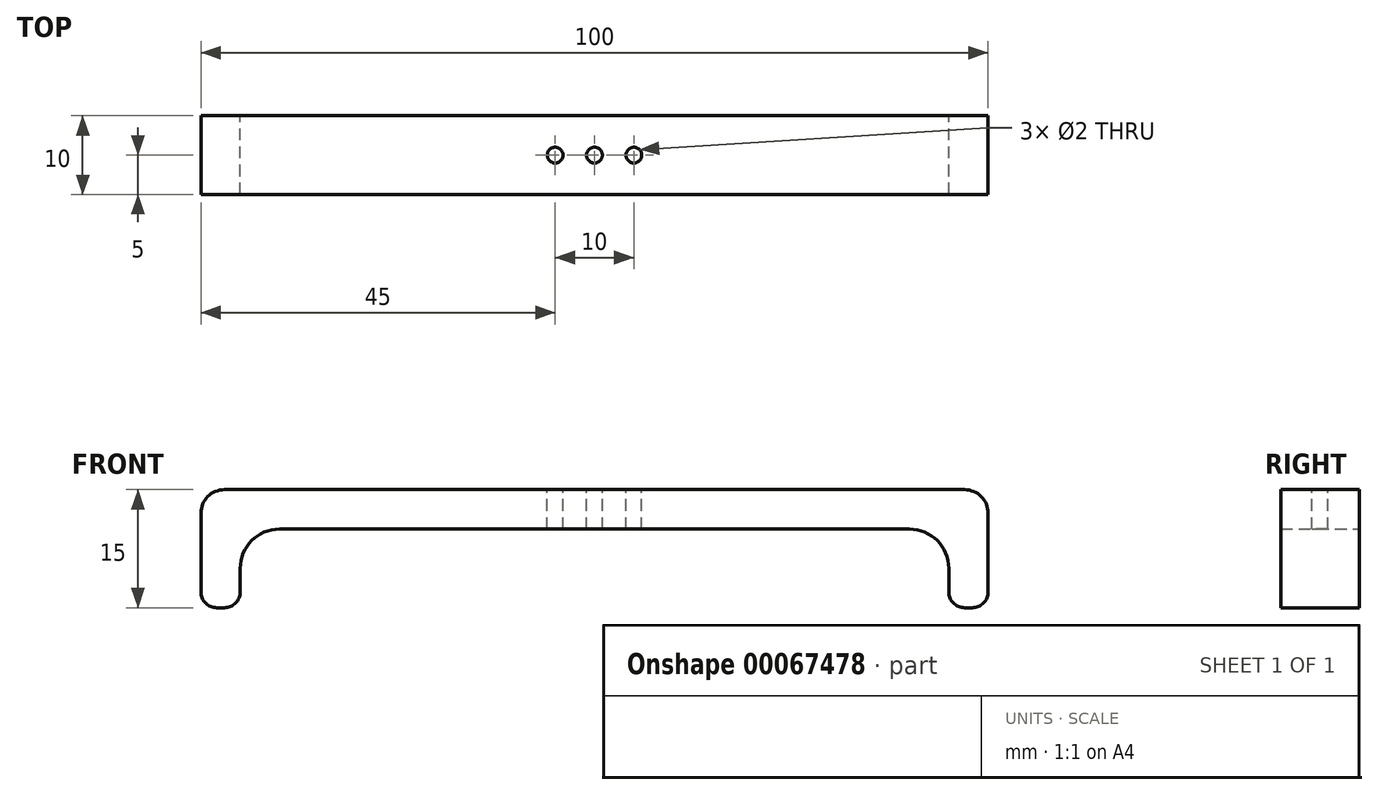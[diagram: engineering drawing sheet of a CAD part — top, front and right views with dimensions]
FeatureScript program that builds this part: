
annotation { "Feature Type Name" : "Feature", "Feature Type Description" : "" }
export const myFeature = defineFeature(function(context is Context, id is Id, definition is map)
    precondition{}
    {
        {
            var Q0;
            Q0=qCreatedBy(makeId("Front.planeOp"),FACE);
            var sketch = newSketch(context, id + "F0", { "sketchPlane" : qUnion([Q0])});
            skLineSegment(sketch, "E0", {"start": v(-48, 0) * mm, "end": v(-47, 0) * mm});
            skLineSegment(sketch, "E1", {"start": v(-45, 2) * mm, "end": v(-45, 5) * mm});
            skLineSegment(sketch, "E2", {"start": v(-40, 10) * mm, "end": v(0, 10) * mm});
            skPoint(sketch, "E3.visualSharp", {"position": v(-45, 0) * mm});
            skArc(sketch, "E3.filletArc", {"start": v(-47, 0) * mm, "mid": v(-45.59, 0.59) * mm, "end": v(-45, 2) * mm});
            skArc(sketch, "E4.filletArc", {"start": v(-40, 10) * mm, "mid": v(-43.54, 8.54) * mm, "end": v(-45, 5) * mm});
            skLineSegment(sketch, "E5", {"start": v(-50, 2) * mm, "end": v(-50, 12) * mm});
            skLineSegment(sketch, "E6", {"start": v(-47, 15) * mm, "end": v(0, 15) * mm});
            skPoint(sketch, "E7.visualSharp", {"position": v(-50, 0) * mm});
            skArc(sketch, "E7.filletArc", {"start": v(-50, 2) * mm, "mid": v(-49.41, 0.59) * mm, "end": v(-48, 0) * mm});
            skPoint(sketch, "E8.visualSharp", {"position": v(-50, 15) * mm});
            skArc(sketch, "E8.filletArc", {"start": v(-47, 15) * mm, "mid": v(-49.12, 14.12) * mm, "end": v(-50, 12) * mm});
            skLineSegment(sketch, "E9.MirrorCS", {"start": v(48, 0) * mm, "end": v(47, 0) * mm});
            skPoint(sketch, "E10.MirrorP", {"position": v(50, 15) * mm});
            skPoint(sketch, "E11.MirrorP", {"position": v(50, 0) * mm});
            skArc(sketch, "E12.MirrorCS", {"start": v(47, 15) * mm, "mid": v(49.12, 14.12) * mm, "end": v(50, 12) * mm});
            skLineSegment(sketch, "E13.MirrorCS", {"start": v(45, 2) * mm, "end": v(45, 5) * mm});
            skArc(sketch, "E14.MirrorCS", {"start": v(50, 2) * mm, "mid": v(49.41, 0.59) * mm, "end": v(48, 0) * mm});
            skLineSegment(sketch, "E15.MirrorCS", {"start": v(47, 15) * mm, "end": v(0, 15) * mm});
            skLineSegment(sketch, "E16.MirrorCS", {"start": v(40, 10) * mm, "end": v(0, 10) * mm});
            skLineSegment(sketch, "E17.MirrorCS", {"start": v(50, 2) * mm, "end": v(50, 12) * mm});
            skPoint(sketch, "E18.MirrorP", {"position": v(45, 0) * mm});
            skArc(sketch, "E19.MirrorCS", {"start": v(47, 0) * mm, "mid": v(45.59, 0.59) * mm, "end": v(45, 2) * mm});
            skArc(sketch, "E20.MirrorCS", {"start": v(40, 10) * mm, "mid": v(43.54, 8.54) * mm, "end": v(45, 5) * mm});
            skSolve(sketch);
        }
        {
            var Q0;
            Q0=makeQuery(id+"F0.imprint","IMPRINT",FACE,{"disambiguationData":[TD([[makeQuery(id+"F0.imprint","IMPRINT",EDGE,{"derivedFrom":sQuery(id+"F0.wireOp",EDGE,"E0")}),1.0]])]});
            extrude(context, id + "F1", {"entities" : qUnion([Q0]), "depth" : 10 * mm});
        }
        {
            var Q0;
            Q0=makeQuery(id+"F1.opExtrude","SWEPT_FACE",FACE,{"disambiguationData":[OSD([sQuery(id+"F0.wireOp",EDGE,"E6"),sQuery(id+"F0.wireOp",EDGE,"E15.MirrorCS")])]});
            var sketch = newSketch(context, id + "F2", { "sketchPlane" : qUnion([Q0])});
            skLineSegment(sketch, "E21", {"start": v(0, 0) * mm, "end": v(0, -10) * mm, "construction": true});
            skLineSegment(sketch, "E22", {"start": v(-5, -5) * mm, "end": v(5, -5) * mm, "construction": true});
            skPoint(sketch, "E22.startSnap0", {"position": v(0, -5) * mm});
            skPoint(sketch, "E23", {"position": v(-5, -5) * mm});
            skPoint(sketch, "E24", {"position": v(5, -5) * mm});
            skSolve(sketch);
        }
        {
            var Q0;
            Q0=sQuery(id+"F2.wireOp",VERTEX,"E23");
            var Q1;
            Q1=sQuery(id+"F2.wireOp",VERTEX,"E24");
            var Q2;
            Q2=sQuery(id+"F2.wireOp",VERTEX,"E22.startSnap0");
            var Q3;
            Q3=makeQuery(id+"F1.opExtrude","SWEPT_BODY",BODY,{"disambiguationData":[OSD([sQuery(id+"F0.wireOp",EDGE,"E0"),sQuery(id+"F0.wireOp",EDGE,"E1"),sQuery(id+"F0.wireOp",EDGE,"E2"),sQuery(id+"F0.wireOp",EDGE,"E3.filletArc"),sQuery(id+"F0.wireOp",EDGE,"E4.filletArc"),sQuery(id+"F0.wireOp",EDGE,"E5"),sQuery(id+"F0.wireOp",EDGE,"E6"),sQuery(id+"F0.wireOp",EDGE,"E7.filletArc"),sQuery(id+"F0.wireOp",EDGE,"E8.filletArc"),sQuery(id+"F0.wireOp",EDGE,"E9.MirrorCS"),sQuery(id+"F0.wireOp",EDGE,"E12.MirrorCS"),sQuery(id+"F0.wireOp",EDGE,"E13.MirrorCS"),sQuery(id+"F0.wireOp",EDGE,"E14.MirrorCS"),sQuery(id+"F0.wireOp",EDGE,"E15.MirrorCS"),sQuery(id+"F0.wireOp",EDGE,"E16.MirrorCS"),sQuery(id+"F0.wireOp",EDGE,"E17.MirrorCS"),sQuery(id+"F0.wireOp",EDGE,"E19.MirrorCS"),sQuery(id+"F0.wireOp",EDGE,"E20.MirrorCS")])]});
            hole(context, id + "F3", {"style" : HoleStyle.SIMPLE, "holeDiameter" : 2 * mm, "endStyle" : HoleEndStyle.THROUGH, "locations" : qUnion([Q0, Q1, Q2]), "scope" : qUnion([Q3])});
        }
    });
